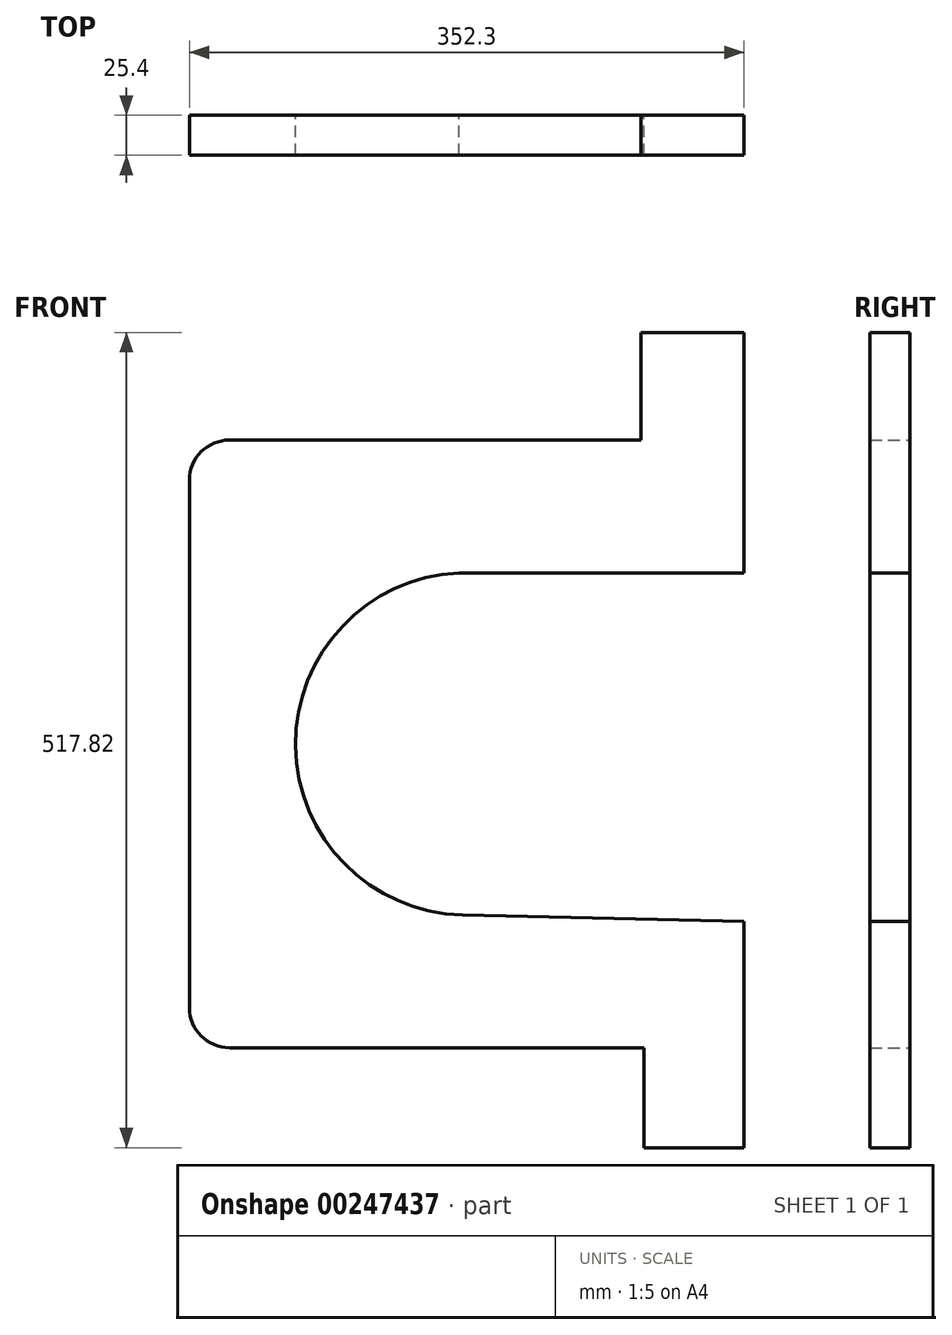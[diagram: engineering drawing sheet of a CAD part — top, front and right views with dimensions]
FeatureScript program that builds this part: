
annotation { "Feature Type Name" : "Feature", "Feature Type Description" : "" }
export const myFeature = defineFeature(function(context is Context, id is Id, definition is map)
    precondition{}
    {
        {
            var Q0;
            Q0=qCreatedBy(makeId("Front.planeOp"),FACE);
            var sketch = newSketch(context, id + "F0", { "sketchPlane" : qUnion([Q0])});
            skLineSegment(sketch, "E0.bottom", {"start": v(-645.09, 324.13) * mm, "end": v(-383.59, 324.13) * mm});
            skLineSegment(sketch, "E0.top", {"start": v(-645.09, -61.84) * mm, "end": v(-381.69, -61.84) * mm});
            skLineSegment(sketch, "E0.left", {"start": v(-670.49, 298.73) * mm, "end": v(-670.49, -36.44) * mm});
            skLineSegment(sketch, "E0.right", {"start": v(-318.19, 324.13) * mm, "end": v(-318.19, 239.78) * mm});
            skArc(sketch, "E1", {"start": v(-489.37, 239.78) * mm, "mid": v(-603.02, 134.9) * mm, "end": v(-496.89, 22.42) * mm});
            skPoint(sketch, "E1.centerSnap0", {"position": v(-318.19, 131.14) * mm});
            skPoint(sketch, "E1.centerSnap1", {"position": v(-494.34, -61.84) * mm});
            skLineSegment(sketch, "E2", {"start": v(-499.3, 239.78) * mm, "end": v(-318.19, 239.78) * mm});
            skLineSegment(sketch, "E3", {"start": v(-496.89, 22.42) * mm, "end": v(-318.19, 18.23) * mm});
            skLineSegment(sketch, "E4.trimOffspring", {"start": v(-318.19, 18.23) * mm, "end": v(-318.19, -61.84) * mm});
            skLineSegment(sketch, "E5.left", {"start": v(-318.19, 324.13) * mm, "end": v(-318.19, 327.94) * mm});
            skLineSegment(sketch, "E5.right", {"start": v(-383.59, 324.13) * mm, "end": v(-383.59, 327.94) * mm});
            skPoint(sketch, "E6.visualSharp", {"position": v(-670.49, 324.13) * mm});
            skArc(sketch, "E7.filletArc", {"start": v(-645.09, 324.13) * mm, "mid": v(-663.05, 316.69) * mm, "end": v(-670.49, 298.73) * mm});
            skPoint(sketch, "E8.visualSharp", {"position": v(-670.49, -61.84) * mm});
            skArc(sketch, "E8.filletArc", {"start": v(-670.49, -36.44) * mm, "mid": v(-663.05, -54.4) * mm, "end": v(-645.09, -61.84) * mm});
            skLineSegment(sketch, "E9.top", {"start": v(-318.19, 392.48) * mm, "end": v(-383.59, 392.48) * mm});
            skLineSegment(sketch, "E9.left", {"start": v(-318.19, 327.94) * mm, "end": v(-318.19, 392.48) * mm});
            skLineSegment(sketch, "E9.right", {"start": v(-383.59, 327.94) * mm, "end": v(-383.59, 392.48) * mm});
            skPoint(sketch, "E10.top.end.orphan", {"position": v(-383.59, -125.34) * mm});
            skLineSegment(sketch, "E11.top", {"start": v(-318.19, -125.34) * mm, "end": v(-381.69, -125.34) * mm});
            skLineSegment(sketch, "E11.left", {"start": v(-318.19, -61.84) * mm, "end": v(-318.19, -125.34) * mm});
            skLineSegment(sketch, "E11.right", {"start": v(-381.69, -61.84) * mm, "end": v(-381.69, -125.34) * mm});
            skSolve(sketch);
        }
        {
            var Q0;
            Q0 = qSketchRegion(id + "F0", true);
            extrude(context, id + "F1", {"entities" : qUnion([Q0]), "depth" : 25.4 * mm});
        }
    });
